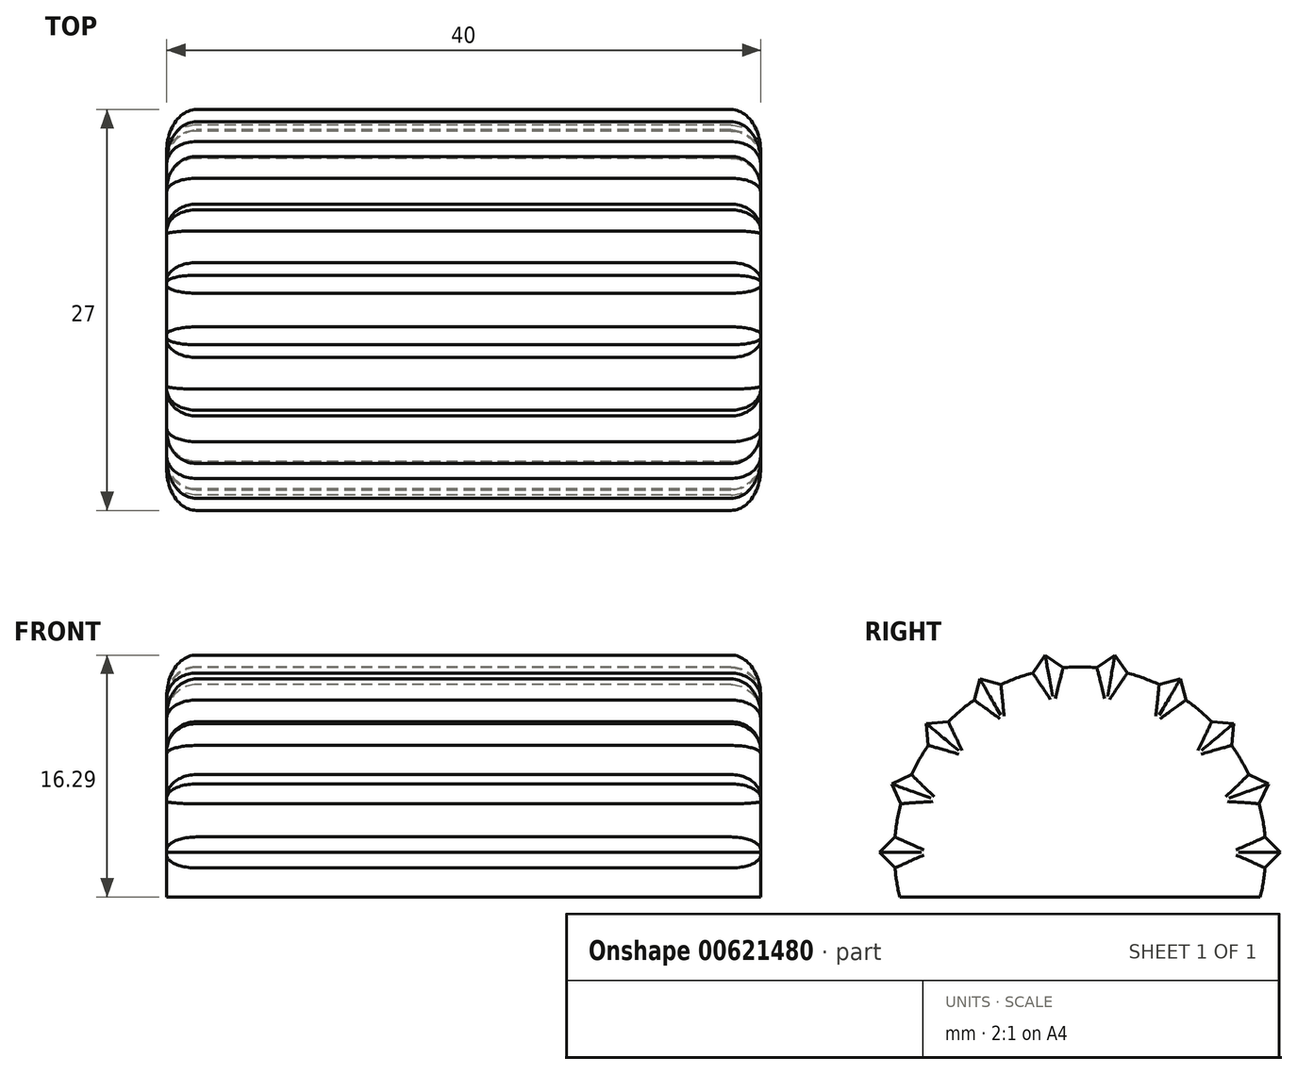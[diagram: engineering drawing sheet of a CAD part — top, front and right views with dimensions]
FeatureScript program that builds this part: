
annotation { "Feature Type Name" : "Feature", "Feature Type Description" : "" }
export const myFeature = defineFeature(function(context is Context, id is Id, definition is map)
    precondition{}
    {
        {
            var Q0;
            Q0=qCreatedBy(makeId("Right.planeOp"),FACE);
            var sketch = newSketch(context, id + "F0", { "sketchPlane" : qUnion([Q0])});
            skArc(sketch, "E0", {"start": v(12.13, -3) * mm, "mid": v(12.33, -2.03) * mm, "end": v(12.46, -1.04) * mm});
            skLineSegment(sketch, "E1", {"start": v(12.13, -3) * mm, "end": v(-12.13, -3) * mm});
            skLineSegment(sketch, "E2", {"start": v(0, 0) * mm, "end": v(-14.18, 0) * mm, "construction": true});
            skLineSegment(sketch, "E3", {"start": v(-12.46, -1.04) * mm, "end": v(-13.5, 0) * mm});
            skLineSegment(sketch, "E4", {"start": v(-13.5, 0) * mm, "end": v(-12.46, 1.04) * mm});
            skLineSegment(sketch, "E5.1.0", {"start": v(-12.69, 4.62) * mm, "end": v(-11.35, 5.24) * mm});
            skLineSegment(sketch, "E5.1.1", {"start": v(-12.06, 3.28) * mm, "end": v(-12.69, 4.62) * mm});
            skLineSegment(sketch, "E5.1.2", {"start": v(0, 0) * mm, "end": v(-13.32, 4.85) * mm, "construction": true});
            skLineSegment(sketch, "E5.2.0", {"start": v(-10.34, 8.68) * mm, "end": v(-8.87, 8.8) * mm});
            skLineSegment(sketch, "E5.2.1", {"start": v(-10.21, 7.2) * mm, "end": v(-10.34, 8.68) * mm});
            skLineSegment(sketch, "E5.2.2", {"start": v(0, 0) * mm, "end": v(-10.86, 9.11) * mm, "construction": true});
            skLineSegment(sketch, "E5.3.0", {"start": v(-6.75, 11.7) * mm, "end": v(-5.32, 11.3) * mm});
            skLineSegment(sketch, "E5.3.1", {"start": v(-7.13, 10.27) * mm, "end": v(-6.75, 11.7) * mm});
            skLineSegment(sketch, "E5.3.2", {"start": v(0, 0) * mm, "end": v(-7.09, 12.28) * mm, "construction": true});
            skLineSegment(sketch, "E5.4.0", {"start": v(-2.34, 13.3) * mm, "end": v(-1.14, 12.45) * mm});
            skLineSegment(sketch, "E5.4.1", {"start": v(-3.2, 12.09) * mm, "end": v(-2.34, 13.3) * mm});
            skLineSegment(sketch, "E5.4.2", {"start": v(0, 0) * mm, "end": v(-2.46, 13.96) * mm, "construction": true});
            skLineSegment(sketch, "E5.5.0", {"start": v(2.34, 13.3) * mm, "end": v(3.2, 12.09) * mm});
            skLineSegment(sketch, "E5.5.1", {"start": v(1.14, 12.45) * mm, "end": v(2.34, 13.3) * mm});
            skLineSegment(sketch, "E5.5.2", {"start": v(0, 0) * mm, "end": v(2.46, 13.96) * mm, "construction": true});
            skLineSegment(sketch, "E5.6.0", {"start": v(6.75, 11.7) * mm, "end": v(7.13, 10.27) * mm});
            skLineSegment(sketch, "E5.6.1", {"start": v(5.32, 11.3) * mm, "end": v(6.75, 11.7) * mm});
            skLineSegment(sketch, "E5.6.2", {"start": v(0, 0) * mm, "end": v(7.09, 12.28) * mm, "construction": true});
            skLineSegment(sketch, "E5.7.0", {"start": v(10.34, 8.68) * mm, "end": v(10.21, 7.2) * mm});
            skLineSegment(sketch, "E5.7.1", {"start": v(8.87, 8.8) * mm, "end": v(10.34, 8.68) * mm});
            skLineSegment(sketch, "E5.7.2", {"start": v(0, 0) * mm, "end": v(10.86, 9.11) * mm, "construction": true});
            skLineSegment(sketch, "E5.8.0", {"start": v(12.69, 4.62) * mm, "end": v(12.06, 3.28) * mm});
            skLineSegment(sketch, "E5.8.1", {"start": v(11.35, 5.24) * mm, "end": v(12.69, 4.62) * mm});
            skLineSegment(sketch, "E5.8.2", {"start": v(0, 0) * mm, "end": v(13.32, 4.85) * mm, "construction": true});
            skLineSegment(sketch, "E5.9.0", {"start": v(13.5, 0) * mm, "end": v(12.46, -1.04) * mm});
            skLineSegment(sketch, "E5.9.1", {"start": v(12.46, 1.04) * mm, "end": v(13.5, 0) * mm});
            skLineSegment(sketch, "E5.9.2", {"start": v(0, 0) * mm, "end": v(14.18, 0) * mm, "construction": true});
            skLineSegment(sketch, "E5.anchor2", {"start": v(0, 0) * mm, "end": v(14.18, 0) * mm, "construction": true});
            skArc(sketch, "E6.trimOffspring", {"start": v(-12.46, -1.04) * mm, "mid": v(-12.33, -2.03) * mm, "end": v(-12.13, -3) * mm});
            skArc(sketch, "E7.trimOffspring", {"start": v(-12.06, 3.28) * mm, "mid": v(-12.31, 2.17) * mm, "end": v(-12.46, 1.04) * mm});
            skArc(sketch, "E8.trimOffspring", {"start": v(-10.21, 7.2) * mm, "mid": v(-10.83, 6.25) * mm, "end": v(-11.35, 5.24) * mm});
            skArc(sketch, "E9.trimOffspring", {"start": v(-7.13, 10.27) * mm, "mid": v(-8.03, 9.58) * mm, "end": v(-8.87, 8.8) * mm});
            skArc(sketch, "E10.trimOffspring", {"start": v(-3.2, 12.09) * mm, "mid": v(-4.28, 11.75) * mm, "end": v(-5.32, 11.3) * mm});
            skArc(sketch, "E11.trimOffspring", {"start": v(1.14, 12.45) * mm, "mid": v(0, 12.5) * mm, "end": v(-1.14, 12.45) * mm});
            skArc(sketch, "E12.trimOffspring", {"start": v(5.32, 11.3) * mm, "mid": v(4.28, 11.75) * mm, "end": v(3.2, 12.09) * mm});
            skArc(sketch, "E13.trimOffspring", {"start": v(8.87, 8.8) * mm, "mid": v(8.03, 9.58) * mm, "end": v(7.13, 10.27) * mm});
            skArc(sketch, "E14.trimOffspring", {"start": v(11.35, 5.24) * mm, "mid": v(10.83, 6.25) * mm, "end": v(10.21, 7.2) * mm});
            skArc(sketch, "E15.trimOffspring", {"start": v(12.46, 1.04) * mm, "mid": v(12.31, 2.17) * mm, "end": v(12.06, 3.28) * mm});
            skSolve(sketch);
        }
        {
            var Q0;
            Q0 = qSketchRegion(id + "F0", true);
            extrude(context, id + "F1", {"entities" : qUnion([Q0]), "depth" : 40 * mm, "offsetDistance" : 25 * mm, "symmetric" : true});
        }
        {
            var Q0;
            Q0=makeQuery(id+"F1.opExtrude","CAP_EDGE",EDGE,{"disambiguationData":[OSD([sQuery(id+"F0.wireOp",EDGE,"E6.trimOffspring")])],"isStart":false});
            var Q1;
            Q1=makeQuery(id+"F1.opExtrude","CAP_EDGE",EDGE,{"disambiguationData":[OSD([sQuery(id+"F0.wireOp",EDGE,"E3")])],"isStart":false});
            var Q2;
            Q2=makeQuery(id+"F1.opExtrude","CAP_EDGE",EDGE,{"disambiguationData":[OSD([sQuery(id+"F0.wireOp",EDGE,"E4")])],"isStart":false});
            var Q3;
            Q3=makeQuery(id+"F1.opExtrude","CAP_EDGE",EDGE,{"disambiguationData":[OSD([sQuery(id+"F0.wireOp",EDGE,"E7.trimOffspring")])],"isStart":false});
            var Q4;
            Q4=makeQuery(id+"F1.opExtrude","CAP_EDGE",EDGE,{"disambiguationData":[OSD([sQuery(id+"F0.wireOp",EDGE,"E5.1.1")])],"isStart":false});
            var Q5;
            Q5=makeQuery(id+"F1.opExtrude","CAP_EDGE",EDGE,{"disambiguationData":[OSD([sQuery(id+"F0.wireOp",EDGE,"E8.trimOffspring")])],"isStart":false});
            var Q6;
            Q6=makeQuery(id+"F1.opExtrude","CAP_EDGE",EDGE,{"disambiguationData":[OSD([sQuery(id+"F0.wireOp",EDGE,"E9.trimOffspring")])],"isStart":false});
            var Q7;
            Q7=makeQuery(id+"F1.opExtrude","CAP_EDGE",EDGE,{"disambiguationData":[OSD([sQuery(id+"F0.wireOp",EDGE,"E10.trimOffspring")])],"isStart":false});
            var Q8;
            Q8=makeQuery(id+"F1.opExtrude","CAP_EDGE",EDGE,{"disambiguationData":[OSD([sQuery(id+"F0.wireOp",EDGE,"E11.trimOffspring")])],"isStart":false});
            var Q9;
            Q9=makeQuery(id+"F1.opExtrude","CAP_EDGE",EDGE,{"disambiguationData":[OSD([sQuery(id+"F0.wireOp",EDGE,"E12.trimOffspring")])],"isStart":false});
            var Q10;
            Q10=makeQuery(id+"F1.opExtrude","CAP_EDGE",EDGE,{"disambiguationData":[OSD([sQuery(id+"F0.wireOp",EDGE,"E13.trimOffspring")])],"isStart":false});
            var Q11;
            Q11=makeQuery(id+"F1.opExtrude","CAP_EDGE",EDGE,{"disambiguationData":[OSD([sQuery(id+"F0.wireOp",EDGE,"E14.trimOffspring")])],"isStart":false});
            var Q12;
            Q12=makeQuery(id+"F1.opExtrude","CAP_EDGE",EDGE,{"disambiguationData":[OSD([sQuery(id+"F0.wireOp",EDGE,"E15.trimOffspring")])],"isStart":false});
            var Q13;
            Q13=makeQuery(id+"F1.opExtrude","CAP_EDGE",EDGE,{"disambiguationData":[OSD([sQuery(id+"F0.wireOp",EDGE,"E0")])],"isStart":false});
            var Q14;
            Q14=makeQuery(id+"F1.opExtrude","CAP_EDGE",EDGE,{"disambiguationData":[OSD([sQuery(id+"F0.wireOp",EDGE,"E5.9.0")])],"isStart":false});
            var Q15;
            Q15=makeQuery(id+"F1.opExtrude","CAP_EDGE",EDGE,{"disambiguationData":[OSD([sQuery(id+"F0.wireOp",EDGE,"E5.9.1")])],"isStart":false});
            var Q16;
            Q16=makeQuery(id+"F1.opExtrude","CAP_EDGE",EDGE,{"disambiguationData":[OSD([sQuery(id+"F0.wireOp",EDGE,"E5.8.0")])],"isStart":false});
            var Q17;
            Q17=makeQuery(id+"F1.opExtrude","CAP_EDGE",EDGE,{"disambiguationData":[OSD([sQuery(id+"F0.wireOp",EDGE,"E5.8.1")])],"isStart":false});
            var Q18;
            Q18=makeQuery(id+"F1.opExtrude","CAP_EDGE",EDGE,{"disambiguationData":[OSD([sQuery(id+"F0.wireOp",EDGE,"E5.7.0")])],"isStart":false});
            var Q19;
            Q19=makeQuery(id+"F1.opExtrude","CAP_EDGE",EDGE,{"disambiguationData":[OSD([sQuery(id+"F0.wireOp",EDGE,"E5.7.1")])],"isStart":false});
            var Q20;
            Q20=makeQuery(id+"F1.opExtrude","CAP_EDGE",EDGE,{"disambiguationData":[OSD([sQuery(id+"F0.wireOp",EDGE,"E5.6.0")])],"isStart":false});
            var Q21;
            Q21=makeQuery(id+"F1.opExtrude","CAP_EDGE",EDGE,{"disambiguationData":[OSD([sQuery(id+"F0.wireOp",EDGE,"E5.6.1")])],"isStart":false});
            var Q22;
            Q22=makeQuery(id+"F1.opExtrude","CAP_EDGE",EDGE,{"disambiguationData":[OSD([sQuery(id+"F0.wireOp",EDGE,"E5.5.0")])],"isStart":false});
            var Q23;
            Q23=makeQuery(id+"F1.opExtrude","CAP_EDGE",EDGE,{"disambiguationData":[OSD([sQuery(id+"F0.wireOp",EDGE,"E5.5.1")])],"isStart":false});
            var Q24;
            Q24=makeQuery(id+"F1.opExtrude","CAP_EDGE",EDGE,{"disambiguationData":[OSD([sQuery(id+"F0.wireOp",EDGE,"E5.4.0")])],"isStart":false});
            var Q25;
            Q25=makeQuery(id+"F1.opExtrude","CAP_EDGE",EDGE,{"disambiguationData":[OSD([sQuery(id+"F0.wireOp",EDGE,"E5.4.1")])],"isStart":false});
            var Q26;
            Q26=makeQuery(id+"F1.opExtrude","CAP_EDGE",EDGE,{"disambiguationData":[OSD([sQuery(id+"F0.wireOp",EDGE,"E5.3.0")])],"isStart":false});
            var Q27;
            Q27=makeQuery(id+"F1.opExtrude","CAP_EDGE",EDGE,{"disambiguationData":[OSD([sQuery(id+"F0.wireOp",EDGE,"E5.3.1")])],"isStart":false});
            var Q28;
            Q28=makeQuery(id+"F1.opExtrude","CAP_EDGE",EDGE,{"disambiguationData":[OSD([sQuery(id+"F0.wireOp",EDGE,"E5.2.0")])],"isStart":false});
            var Q29;
            Q29=makeQuery(id+"F1.opExtrude","CAP_EDGE",EDGE,{"disambiguationData":[OSD([sQuery(id+"F0.wireOp",EDGE,"E5.2.1")])],"isStart":false});
            var Q30;
            Q30=makeQuery(id+"F1.opExtrude","CAP_EDGE",EDGE,{"disambiguationData":[OSD([sQuery(id+"F0.wireOp",EDGE,"E5.1.0")])],"isStart":false});
            var Q31;
            Q31=makeQuery(id+"F1.opExtrude","CAP_EDGE",EDGE,{"disambiguationData":[OSD([sQuery(id+"F0.wireOp",EDGE,"E0")])],"isStart":true});
            var Q32;
            Q32=makeQuery(id+"F1.opExtrude","CAP_EDGE",EDGE,{"disambiguationData":[OSD([sQuery(id+"F0.wireOp",EDGE,"E15.trimOffspring")])],"isStart":true});
            var Q33;
            Q33=makeQuery(id+"F1.opExtrude","CAP_EDGE",EDGE,{"disambiguationData":[OSD([sQuery(id+"F0.wireOp",EDGE,"E14.trimOffspring")])],"isStart":true});
            var Q34;
            Q34=makeQuery(id+"F1.opExtrude","CAP_EDGE",EDGE,{"disambiguationData":[OSD([sQuery(id+"F0.wireOp",EDGE,"E13.trimOffspring")])],"isStart":true});
            var Q35;
            Q35=makeQuery(id+"F1.opExtrude","CAP_EDGE",EDGE,{"disambiguationData":[OSD([sQuery(id+"F0.wireOp",EDGE,"E12.trimOffspring")])],"isStart":true});
            var Q36;
            Q36=makeQuery(id+"F1.opExtrude","CAP_EDGE",EDGE,{"disambiguationData":[OSD([sQuery(id+"F0.wireOp",EDGE,"E11.trimOffspring")])],"isStart":true});
            var Q37;
            Q37=makeQuery(id+"F1.opExtrude","CAP_EDGE",EDGE,{"disambiguationData":[OSD([sQuery(id+"F0.wireOp",EDGE,"E10.trimOffspring")])],"isStart":true});
            var Q38;
            Q38=makeQuery(id+"F1.opExtrude","CAP_EDGE",EDGE,{"disambiguationData":[OSD([sQuery(id+"F0.wireOp",EDGE,"E9.trimOffspring")])],"isStart":true});
            var Q39;
            Q39=makeQuery(id+"F1.opExtrude","CAP_EDGE",EDGE,{"disambiguationData":[OSD([sQuery(id+"F0.wireOp",EDGE,"E8.trimOffspring")])],"isStart":true});
            var Q40;
            Q40=makeQuery(id+"F1.opExtrude","CAP_EDGE",EDGE,{"disambiguationData":[OSD([sQuery(id+"F0.wireOp",EDGE,"E7.trimOffspring")])],"isStart":true});
            var Q41;
            Q41=makeQuery(id+"F1.opExtrude","CAP_EDGE",EDGE,{"disambiguationData":[OSD([sQuery(id+"F0.wireOp",EDGE,"E6.trimOffspring")])],"isStart":true});
            var Q42;
            Q42=makeQuery(id+"F1.opExtrude","CAP_EDGE",EDGE,{"disambiguationData":[OSD([sQuery(id+"F0.wireOp",EDGE,"E3")])],"isStart":true});
            var Q43;
            Q43=makeQuery(id+"F1.opExtrude","CAP_EDGE",EDGE,{"disambiguationData":[OSD([sQuery(id+"F0.wireOp",EDGE,"E4")])],"isStart":true});
            var Q44;
            Q44=makeQuery(id+"F1.opExtrude","CAP_EDGE",EDGE,{"disambiguationData":[OSD([sQuery(id+"F0.wireOp",EDGE,"E5.1.1")])],"isStart":true});
            var Q45;
            Q45=makeQuery(id+"F1.opExtrude","CAP_EDGE",EDGE,{"disambiguationData":[OSD([sQuery(id+"F0.wireOp",EDGE,"E5.1.0")])],"isStart":true});
            var Q46;
            Q46=makeQuery(id+"F1.opExtrude","CAP_EDGE",EDGE,{"disambiguationData":[OSD([sQuery(id+"F0.wireOp",EDGE,"E5.2.1")])],"isStart":true});
            var Q47;
            Q47=makeQuery(id+"F1.opExtrude","CAP_EDGE",EDGE,{"disambiguationData":[OSD([sQuery(id+"F0.wireOp",EDGE,"E5.2.0")])],"isStart":true});
            var Q48;
            Q48=makeQuery(id+"F1.opExtrude","CAP_EDGE",EDGE,{"disambiguationData":[OSD([sQuery(id+"F0.wireOp",EDGE,"E5.3.1")])],"isStart":true});
            var Q49;
            Q49=makeQuery(id+"F1.opExtrude","CAP_EDGE",EDGE,{"disambiguationData":[OSD([sQuery(id+"F0.wireOp",EDGE,"E5.3.0")])],"isStart":true});
            var Q50;
            Q50=makeQuery(id+"F1.opExtrude","CAP_EDGE",EDGE,{"disambiguationData":[OSD([sQuery(id+"F0.wireOp",EDGE,"E5.4.1")])],"isStart":true});
            var Q51;
            Q51=makeQuery(id+"F1.opExtrude","CAP_EDGE",EDGE,{"disambiguationData":[OSD([sQuery(id+"F0.wireOp",EDGE,"E5.4.0")])],"isStart":true});
            var Q52;
            Q52=makeQuery(id+"F1.opExtrude","CAP_EDGE",EDGE,{"disambiguationData":[OSD([sQuery(id+"F0.wireOp",EDGE,"E5.5.1")])],"isStart":true});
            var Q53;
            Q53=makeQuery(id+"F1.opExtrude","CAP_EDGE",EDGE,{"disambiguationData":[OSD([sQuery(id+"F0.wireOp",EDGE,"E5.5.0")])],"isStart":true});
            var Q54;
            Q54=makeQuery(id+"F1.opExtrude","CAP_EDGE",EDGE,{"disambiguationData":[OSD([sQuery(id+"F0.wireOp",EDGE,"E5.6.1")])],"isStart":true});
            var Q55;
            Q55=makeQuery(id+"F1.opExtrude","CAP_EDGE",EDGE,{"disambiguationData":[OSD([sQuery(id+"F0.wireOp",EDGE,"E5.6.0")])],"isStart":true});
            var Q56;
            Q56=makeQuery(id+"F1.opExtrude","CAP_EDGE",EDGE,{"disambiguationData":[OSD([sQuery(id+"F0.wireOp",EDGE,"E5.7.1")])],"isStart":true});
            var Q57;
            Q57=makeQuery(id+"F1.opExtrude","CAP_EDGE",EDGE,{"disambiguationData":[OSD([sQuery(id+"F0.wireOp",EDGE,"E5.7.0")])],"isStart":true});
            var Q58;
            Q58=makeQuery(id+"F1.opExtrude","CAP_EDGE",EDGE,{"disambiguationData":[OSD([sQuery(id+"F0.wireOp",EDGE,"E5.8.1")])],"isStart":true});
            var Q59;
            Q59=makeQuery(id+"F1.opExtrude","CAP_EDGE",EDGE,{"disambiguationData":[OSD([sQuery(id+"F0.wireOp",EDGE,"E5.8.0")])],"isStart":true});
            var Q60;
            Q60=makeQuery(id+"F1.opExtrude","CAP_EDGE",EDGE,{"disambiguationData":[OSD([sQuery(id+"F0.wireOp",EDGE,"E5.9.1")])],"isStart":true});
            var Q61;
            Q61=makeQuery(id+"F1.opExtrude","CAP_EDGE",EDGE,{"disambiguationData":[OSD([sQuery(id+"F0.wireOp",EDGE,"E5.9.0")])],"isStart":true});
            fillet(context, id + "F2", {"entities" : qUnion([Q0, Q1, Q2, Q3, Q4, Q5, Q6, Q7, Q8, Q9, Q10, Q11, Q12, Q13, Q14, Q15, Q16, Q17, Q18, Q19, Q20, Q21, Q22, Q23, Q24, Q25, Q26, Q27, Q28, Q29, Q30, Q31, Q32, Q33, Q34, Q35, Q36, Q37, Q38, Q39, Q40, Q41, Q42, Q43, Q44, Q45, Q46, Q47, Q48, Q49, Q50, Q51, Q52, Q53, Q54, Q55, Q56, Q57, Q58, Q59, Q60, Q61]), "radius" : 2 * mm, "tangentPropagation" : true, "allowEdgeOverflow" : false});
        }
    });
